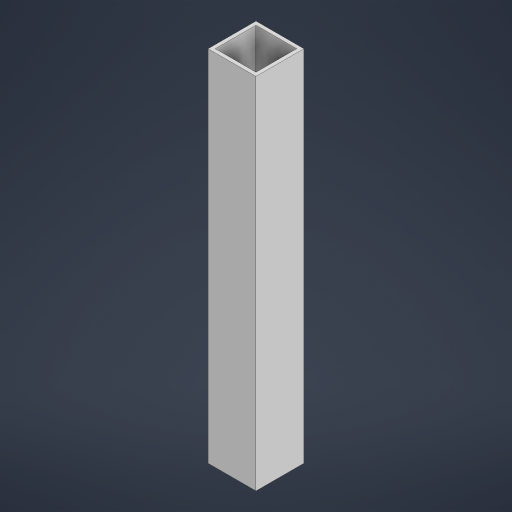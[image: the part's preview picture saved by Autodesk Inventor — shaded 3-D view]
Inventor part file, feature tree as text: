
AUTODESK INVENTOR PART (.ipt)
format: ipt  version: 2024 (Build 280153000, 153)  size: 167,424 bytes
history: native  units: mm
features: other x1, extrude x1, sketch x1
ambient origin geometry x8: Origin, YZ Plane, XZ Plane, XY Plane, X Axis, Y Axis, Z Axis, Center Point
bodies: Body1 (feature_tree)
feature tree (3):
  other  "Твердое тело1"
  extrude  "Выдавливание1"  Depth=20.0mm
  sketch  "Эскиз1"
